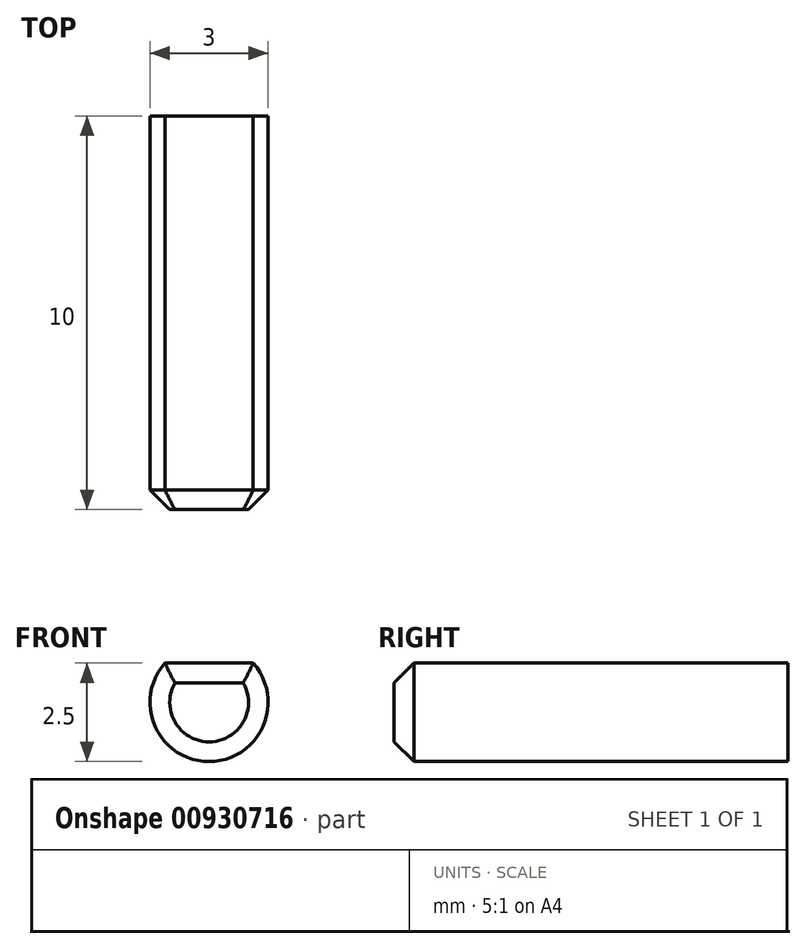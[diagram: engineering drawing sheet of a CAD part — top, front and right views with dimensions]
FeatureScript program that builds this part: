
annotation { "Feature Type Name" : "Feature", "Feature Type Description" : "" }
export const myFeature = defineFeature(function(context is Context, id is Id, definition is map)
    precondition{}
    {
        {
            var Q0;
            Q0=qCreatedBy(makeId("Front.planeOp"),FACE);
            var sketch = newSketch(context, id + "F0", { "sketchPlane" : qUnion([Q0])});
            skArc(sketch, "E0", {"start": v(-1.12, 1) * mm, "mid": v(0, -1.5) * mm, "end": v(1.12, 1) * mm});
            skLineSegment(sketch, "E1.bottom", {"start": v(1.12, 1) * mm, "end": v(-1.12, 1) * mm});
            skPoint(sketch, "E2.orphan", {"position": v(-1.5, 1) * mm});
            skPoint(sketch, "E3.orphan", {"position": v(-1.5, -1) * mm});
            skPoint(sketch, "E4.orphan", {"position": v(1.5, -1) * mm});
            skPoint(sketch, "E5.orphan", {"position": v(1.5, 1) * mm});
            skSolve(sketch);
        }
        {
            var Q0;
            {var subQ0=sQuery(id+"F0.wireOp",EDGE,"E0");var subQ4=sQuery(id+"F0.wireOp",EDGE,"E1.bottom");var subQ8=makeQuery(id+"F0.imprint","INTERSECT",VERTEX,{"disambiguationData":[OD(0.0)],"derivedFrom":[subQ0,subQ4]});Q0=makeQuery(id+"F0.imprint","IMPRINT",FACE,{"disambiguationData":[TD([[makeQuery(id+"F0.imprint","IMPRINT",EDGE,{"disambiguationData":[TD([[subQ8,1.0]])],"derivedFrom":subQ0}),1.0]])]});}
            var Q1;
            {var subQ0=sQuery(id+"F0.wireOp",EDGE,"E1.top");var subQ1=sQuery(id+"F0.wireOp",EDGE,"E0");var subQ2=makeQuery(id+"F0.imprint","INTERSECT",VERTEX,{"disambiguationData":[OD(0.0)],"derivedFrom":[subQ1,subQ0]});Q1=makeQuery(id+"F0.imprint","IMPRINT",FACE,{"disambiguationData":[TD([[makeQuery(id+"F0.imprint","IMPRINT",EDGE,{"disambiguationData":[TD([[subQ2,-1.0]])],"derivedFrom":subQ1}),1.0]])]});}
            extrude(context, id + "F1", {"entities" : qUnion([Q0, Q1]), "depth" : 10 * mm, "offsetDistance" : 25 * mm});
        }
        {
            var Q0;
            Q0=makeQuery(id+"F1.opExtrude","CAP_EDGE",EDGE,{"disambiguationData":[OSD([sQuery(id+"F0.wireOp",EDGE,"E1.bottom")])],"isStart":false});
            var Q1;
            Q1=makeQuery(id+"F1.opExtrude","CAP_EDGE",EDGE,{"disambiguationData":[OSD([sQuery(id+"F0.wireOp",EDGE,"E0")])],"isStart":false});
            chamfer(context, id + "F2", {"entities" : qUnion([Q0, Q1]), "width" : 0.5 * mm, "tangentPropagation" : true});
        }
    });
